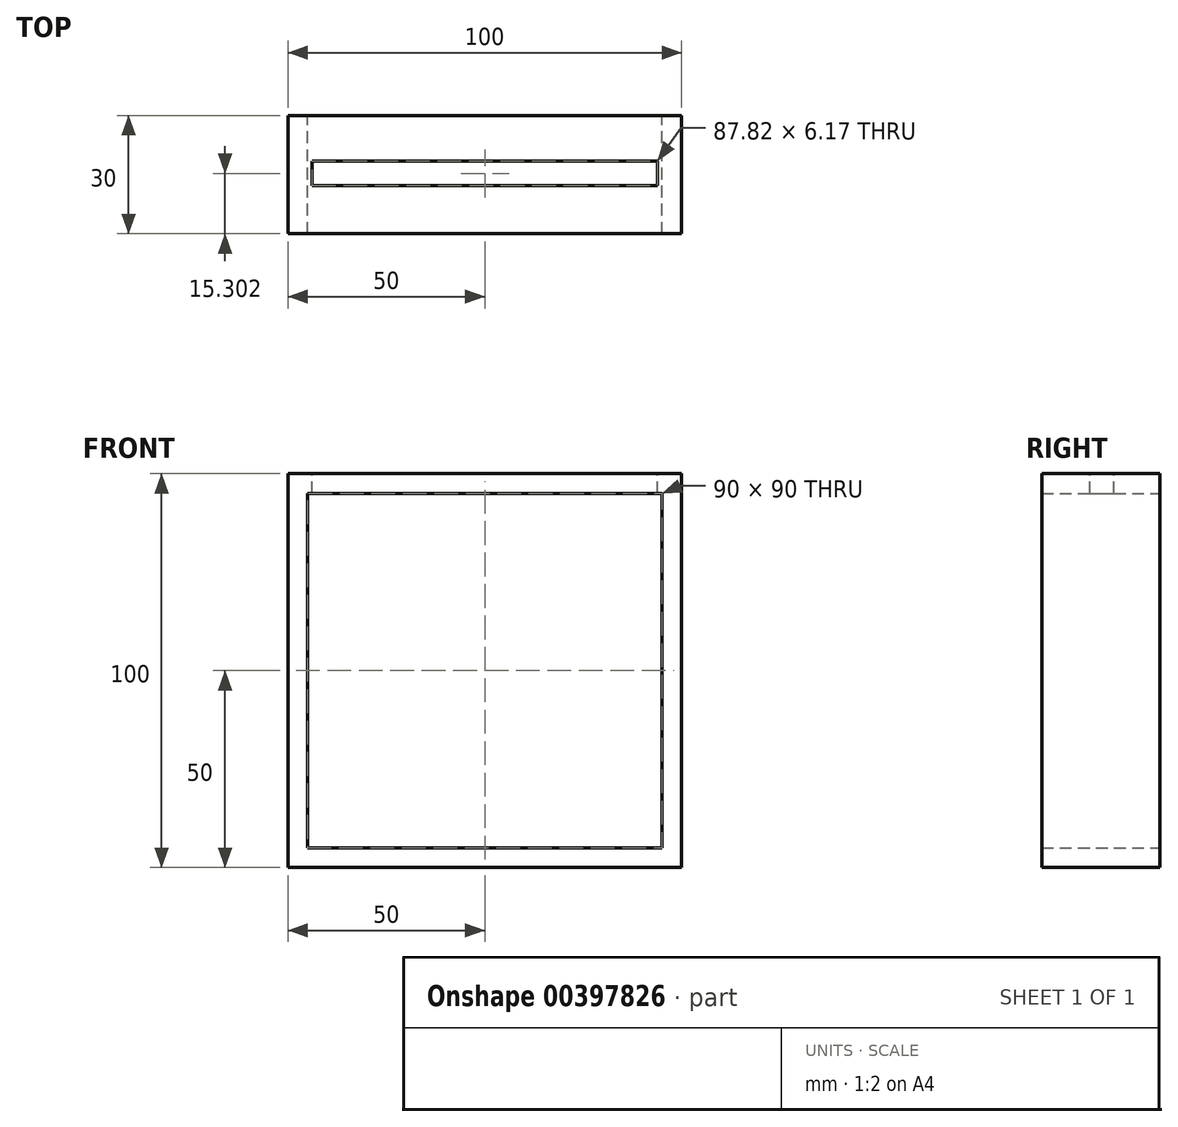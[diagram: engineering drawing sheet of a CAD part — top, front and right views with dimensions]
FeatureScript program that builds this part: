
annotation { "Feature Type Name" : "Feature", "Feature Type Description" : "" }
export const myFeature = defineFeature(function(context is Context, id is Id, definition is map)
    precondition{}
    {
        {
            var Q0;
            Q0=qCreatedBy(makeId("Front.planeOp"),FACE);
            var sketch = newSketch(context, id + "F0", { "sketchPlane" : qUnion([Q0])});
            skLineSegment(sketch, "E0.bottom", {"start": v(-50, 50) * mm, "end": v(50, 50) * mm});
            skLineSegment(sketch, "E0.top", {"start": v(-50, -50) * mm, "end": v(50, -50) * mm});
            skLineSegment(sketch, "E0.left", {"start": v(-50, 50) * mm, "end": v(-50, -50) * mm});
            skLineSegment(sketch, "E0.right", {"start": v(50, 50) * mm, "end": v(50, -50) * mm});
            skPoint(sketch, "E0.middle", {"position": v(0, 0) * mm});
            skLineSegment(sketch, "E1.bottom", {"start": v(-45, 45) * mm, "end": v(45, 45) * mm});
            skLineSegment(sketch, "E1.top", {"start": v(-45, -45) * mm, "end": v(45, -45) * mm});
            skLineSegment(sketch, "E1.left", {"start": v(-45, 45) * mm, "end": v(-45, -45) * mm});
            skLineSegment(sketch, "E1.right", {"start": v(45, 45) * mm, "end": v(45, -45) * mm});
            skSolve(sketch);
        }
        {
            var Q0;
            Q0=makeQuery(id+"F0.imprint","IMPRINT",FACE,{"disambiguationData":[TD([[makeQuery(id+"F0.imprint","IMPRINT",EDGE,{"derivedFrom":sQuery(id+"F0.wireOp",EDGE,"E0.bottom")}),-1.0]])]});
            extrude(context, id + "F1", {"entities" : qUnion([Q0]), "depth" : 30 * mm});
        }
        {
            var Q0;
            Q0=makeQuery(id+"F1.opExtrude","SWEPT_FACE",FACE,{"disambiguationData":[OSD([sQuery(id+"F0.wireOp",EDGE,"E0.bottom")])]});
            var sketch = newSketch(context, id + "F2", { "sketchPlane" : qUnion([Q0])});
            skLineSegment(sketch, "E2.bottom", {"start": v(43.91, -17.78) * mm, "end": v(-43.91, -17.78) * mm});
            skLineSegment(sketch, "E2.top", {"start": v(43.91, -11.61) * mm, "end": v(-43.91, -11.61) * mm});
            skLineSegment(sketch, "E2.left", {"start": v(43.91, -17.78) * mm, "end": v(43.91, -11.61) * mm});
            skLineSegment(sketch, "E2.right", {"start": v(-43.91, -17.78) * mm, "end": v(-43.91, -11.61) * mm});
            skPoint(sketch, "E2.middle", {"position": v(0, -14.7) * mm});
            skSolve(sketch);
        }
        {
            var Q0;
            Q0=makeQuery(id+"F2.imprint","IMPRINT",FACE,{"disambiguationData":[TD([[makeQuery(id+"F2.imprint","IMPRINT",EDGE,{"derivedFrom":sQuery(id+"F2.wireOp",EDGE,"E2.bottom")}),-1.0]])]});
            extrude(context, id + "F3", {"entities" : qUnion([Q0]), "operationType" : NewBodyOperationType.REMOVE, "oppositeDirection" : true, "depth" : 25 * mm});
        }
    });
